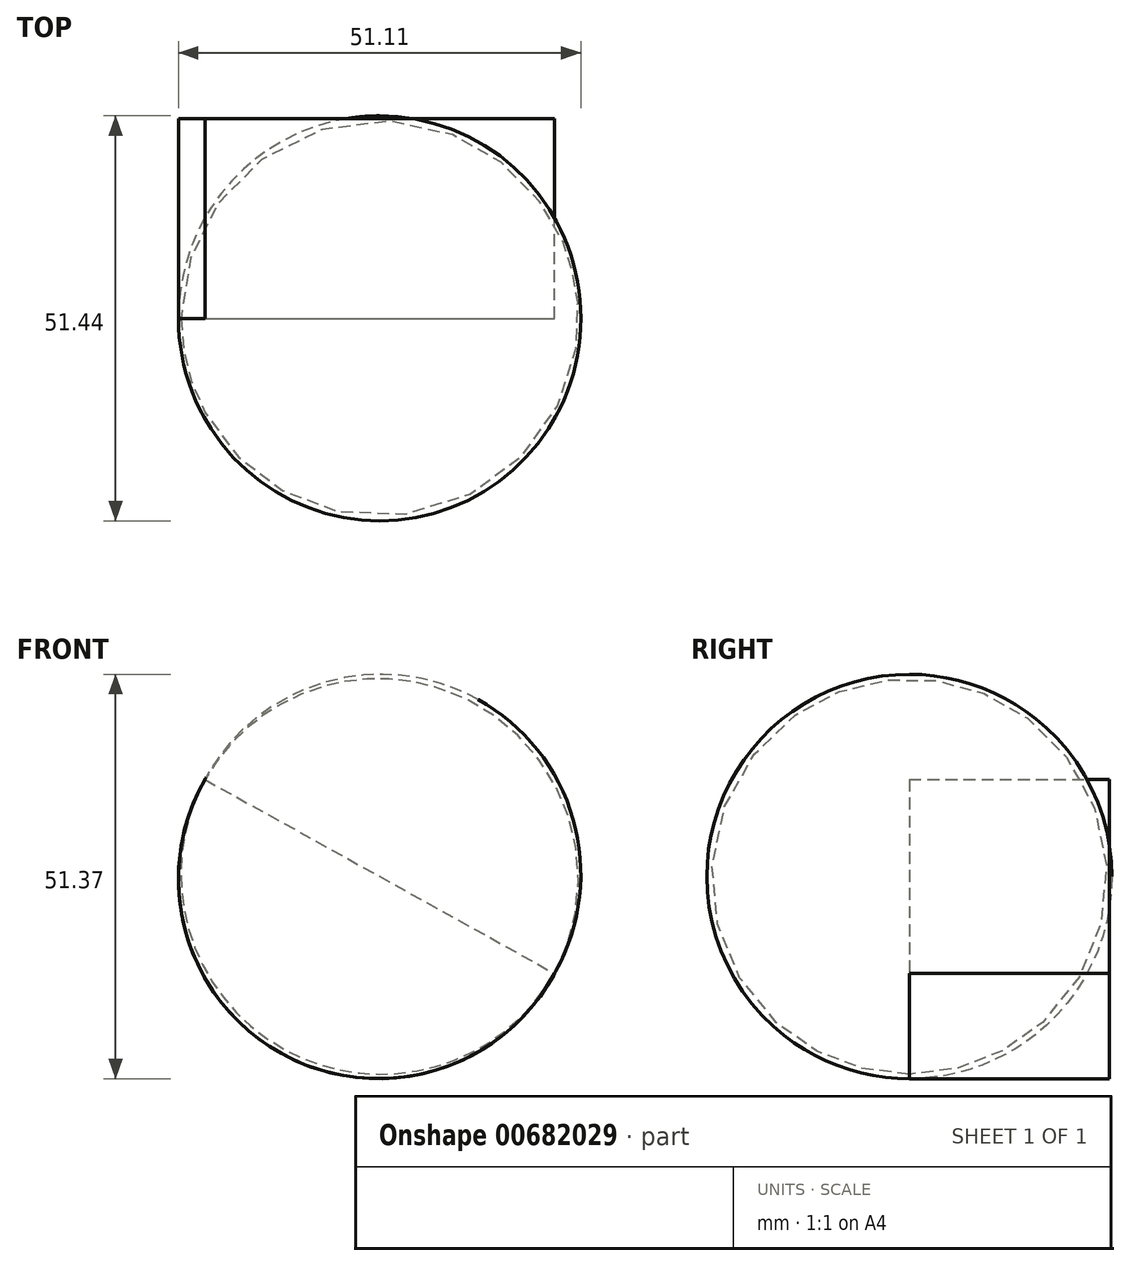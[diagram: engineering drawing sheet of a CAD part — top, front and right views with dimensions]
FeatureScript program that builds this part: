
annotation { "Feature Type Name" : "Feature", "Feature Type Description" : "" }
export const myFeature = defineFeature(function(context is Context, id is Id, definition is map)
    precondition{}
    {
        {
            var Q0;
            Q0=qCreatedBy(makeId("Front.planeOp"),FACE);
            var sketch = newSketch(context, id + "F0", { "sketchPlane" : qUnion([Q0])});
            skArc(sketch, "E0", {"start": v(-22.05, 12.6) * mm, "mid": v(-12.32, -22.21) * mm, "end": v(22.37, -12.04) * mm});
            skLineSegment(sketch, "E1", {"start": v(-22.05, 12.6) * mm, "end": v(22.37, -12.04) * mm});
            skSolve(sketch);
        }
        {
            var Q0;
            Q0 = qSketchRegion(id + "F0", true);
            extrude(context, id + "F1", {"entities" : qUnion([Q0]), "depth" : 25.4 * mm, "offsetDistance" : 25.4 * mm});
        }
        {
            var Q0;
            Q0=makeQuery(id+"F1.opExtrude","CAP_FACE",FACE,{"disambiguationData":[OSD([sQuery(id+"F0.wireOp",EDGE,"E0"),sQuery(id+"F0.wireOp",EDGE,"E1")])],"isStart":false});
            var Q1;
            Q1=makeQuery(id+"F1.opExtrude","CAP_EDGE",EDGE,{"disambiguationData":[OSD([sQuery(id+"F0.wireOp",EDGE,"E1")])],"isStart":false});
            revolve(context, id + "F2", {"entities" : qUnion([Q0]), "axis" : qUnion([Q1]), "revolveType" : RevolveType.FULL});
        }
    });
